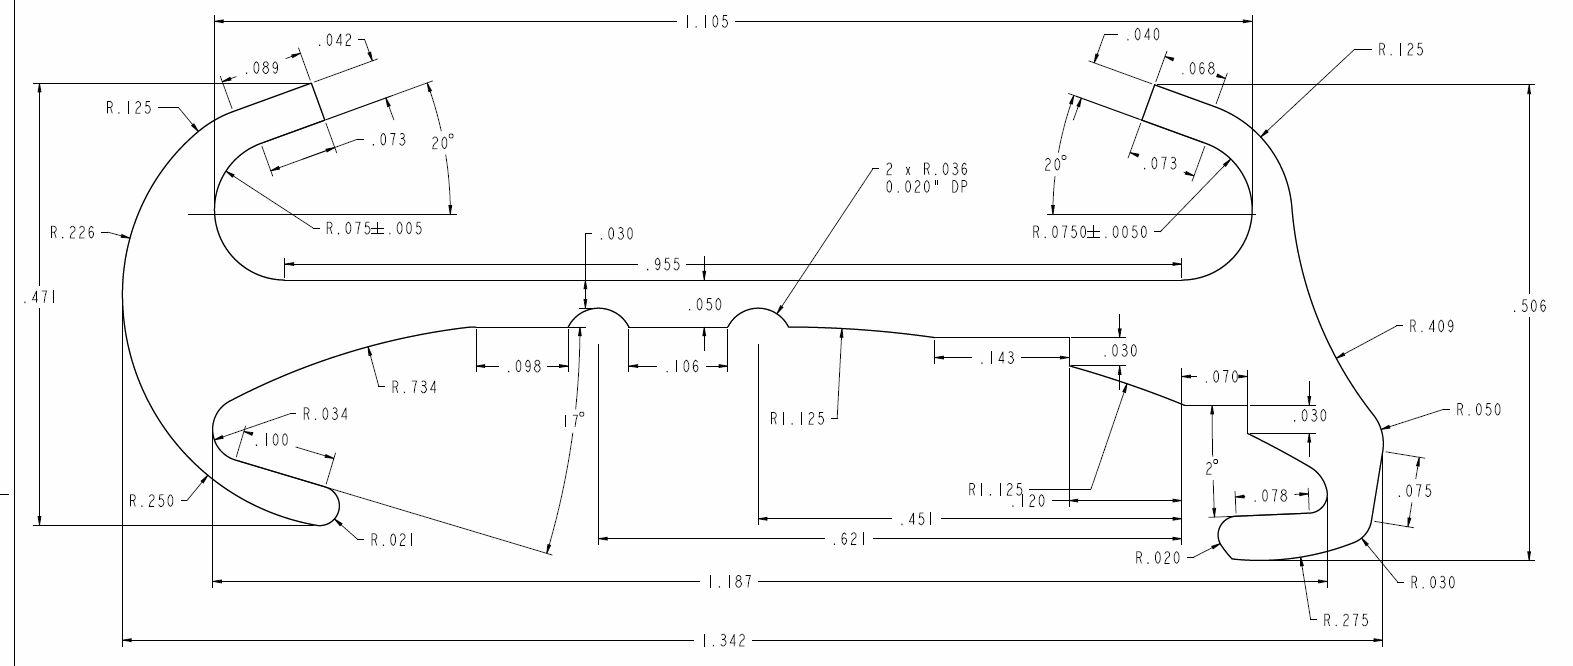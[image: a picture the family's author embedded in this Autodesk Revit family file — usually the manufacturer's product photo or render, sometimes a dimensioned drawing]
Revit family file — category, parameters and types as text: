
# Revit family: O2.5UM-NRG 12' SUSHI
name_source: partatom
category: Mechanical Equipment
revit_build: Autodesk Revit 2017 (Build: 20190508_0315(x64)
units: mm (PartAtom-declared; Revit-internal decimal feet)

## family parameters
Always vertical = Yes
Cut with Voids When Loaded = No
OmniClass Number = 23.40.40.11.17
OmniClass Title = Refrigerated Cases
Part Type = Normal
Room Calculation Point = No
Round Connector Dimension = Use Radius
Shared = No
Work Plane-Based = Yes

## types (1)
- O2.5UM-NRG 12' SUSHI
    12" Shelf = Yes
    18" Shelf = Yes
    Aluminum Frame = <By Category>
    BOTTOM ELECTRICAL = Yes
    BOTTOM REFRIGERATION PIPING = Yes
    Certifications = NSF 7, UL471, CSA
    DATE = 06/18/2020
    DESIGNERS NAME = T.A.G
    DRAIN LINE = 36"
    DRAIN PIPING = Yes
    Default Elevation = 48"
    Description = Multi-Deck Merchandiser with Synerg-E™
    EQUIPMENT DESCRIPTION = Multi-Deck Merchandiser with Synerg-E™
    EQUIPMENT MARK = O2.5UM-NRG Sushi
    Ends = Yes
    GLASS = Glass
    Glass = Glass
    Height = 44 1/8"
    High Power (Cornice) Amps = 0 A
    High Power (Cornice) Watts = 30 W
    How Many Defrosts Per Day = 6
    Island  Case Length = 72"
    Island Application = Dairy / Deli / Produce
    Island BTUH Conventional = 858
    Island BTUH Parallel = 750
    Island Discharge Air Velocity (FPM) = 180 FPM
    Island Discharge Air(°F) = 31 °F
    Island Evaporator (°F) = 28 °F
    Island Fans Per Case = 2
    Island Front Sill Height = All
    Island High Efficiency Fans Amps = 0 A
    Island High Efficiency Fans Watts = 22 W
    Island Superheat @ Bulb Set Point (°F) = 6-8 °F
    Island Timed-Off Fail-Safe (Min) = 30 (Min)
    Island Timed-Off Termination Temp (°F) = 42 °F
    Item Description = Multi-Deck Merchandiser with Synerg-E™
    LF STD END = Yes
    Left KP End = No
    Legend Number = O2.5UM-NRG Sushi
    Length = 144"
    Light Length = 36"
    Lights = CHARCOAL BROWN
    Lights Per Row = 2
    Manufacturer = HILL PHOENIX
    Model = O2.5UM-NRG Sushi
    Number of Shelf = 3
    PAINTED METAL UPPER SHELF = PAINTED SHELVES
    REAR REFRIGERATION PIPING = Yes
    RT KP End = No
    RT STD END = Yes
    Refgn = 12 3/8"
    Shelf distance = 36"
    Standard Power Amps = 14 A
    Standard Power Watts = 17 W
    TOP ELECTRICAL = Yes
    TOP REFRIGERATION PIPING = Yes
    URL = http://www.hillphoenix.com Sushi
    Width = 43 1/4"

## geometry (parser evidence)
native form markers: Blend x11, Sweep x23
no freeform markers — native parametric forms only
